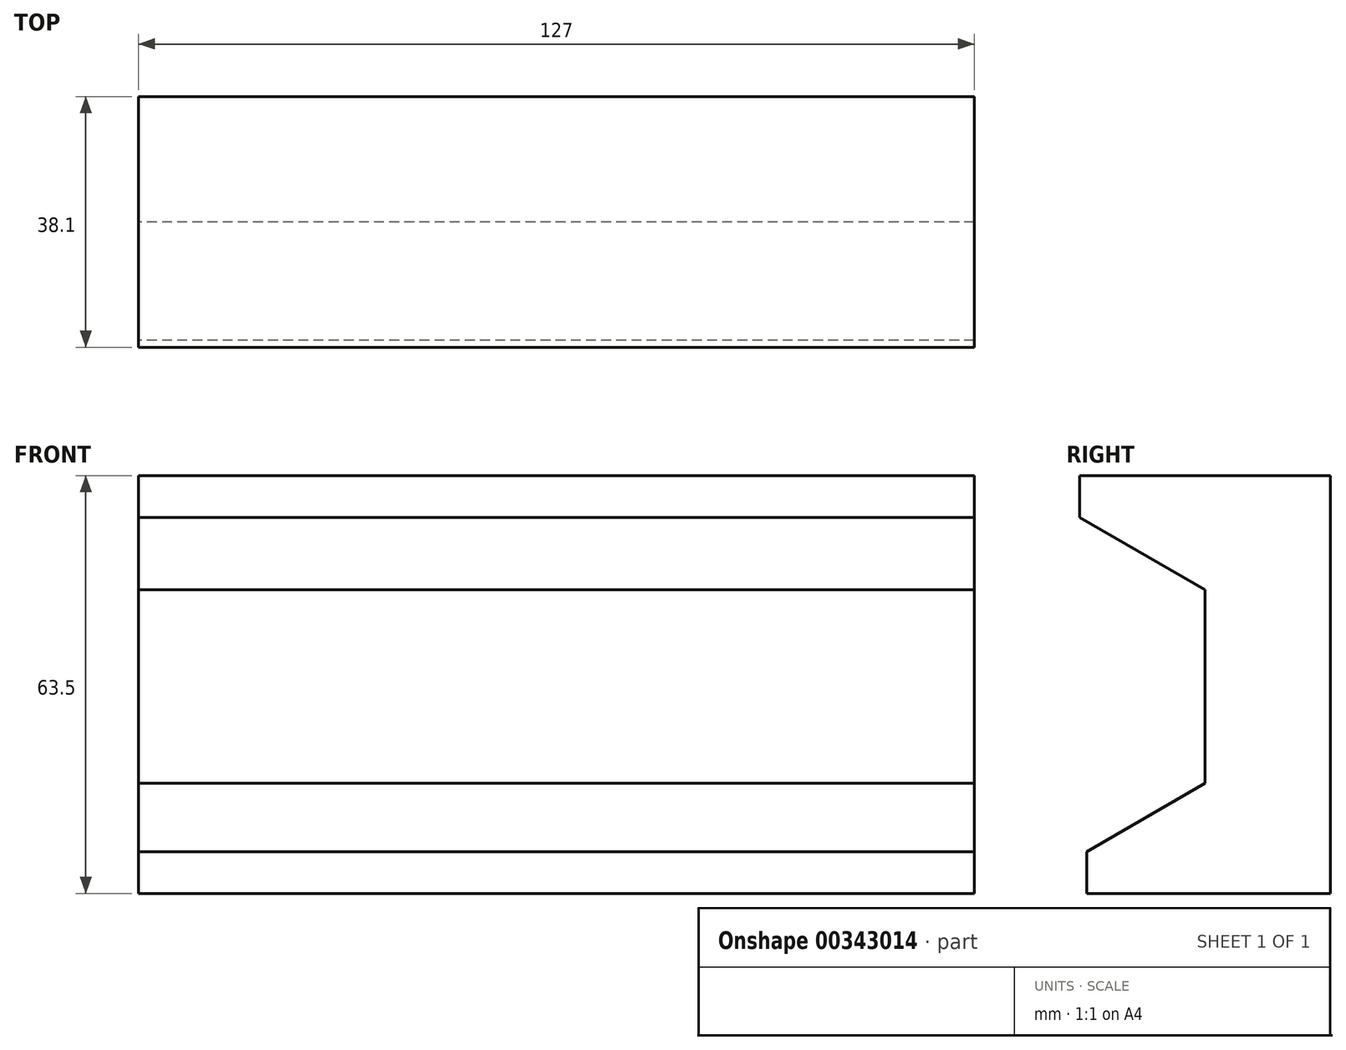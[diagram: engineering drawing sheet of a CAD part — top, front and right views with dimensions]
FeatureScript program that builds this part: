
annotation { "Feature Type Name" : "Feature", "Feature Type Description" : "" }
export const myFeature = defineFeature(function(context is Context, id is Id, definition is map)
    precondition{}
    {
        {
            var Q0;
            Q0=qCreatedBy(makeId("Right.planeOp"),FACE);
            var sketch = newSketch(context, id + "F0", { "sketchPlane" : qUnion([Q0])});
            skLineSegment(sketch, "E0", {"start": v(28.67, 46.63) * mm, "end": v(28.67, -16.87) * mm});
            skLineSegment(sketch, "E1", {"start": v(28.67, 46.63) * mm, "end": v(-9.43, 46.63) * mm});
            skLineSegment(sketch, "E2", {"start": v(28.67, -16.87) * mm, "end": v(-8.37, -16.87) * mm});
            skLineSegment(sketch, "E3", {"start": v(-8.37, -16.87) * mm, "end": v(-8.37, -10.52) * mm});
            skLineSegment(sketch, "E4", {"start": v(-9.43, 46.63) * mm, "end": v(-9.43, 40.28) * mm});
            skLineSegment(sketch, "E5", {"start": v(-9.43, 40.28) * mm, "end": v(9.62, 29.28) * mm});
            skLineSegment(sketch, "E6", {"start": v(9.62, 29.28) * mm, "end": v(9.62, -0.13) * mm});
            skLineSegment(sketch, "E7", {"start": v(9.62, -0.13) * mm, "end": v(-8.37, -10.52) * mm});
            skPoint(sketch, "E8.start.orphan", {"position": v(9.62, 40.28) * mm});
            skSolve(sketch);
        }
        {
            var Q0;
            Q0 = qSketchRegion(id + "F0", true);
            extrude(context, id + "F1", {"entities" : qUnion([Q0]), "depth" : 127 * mm});
        }
    });
